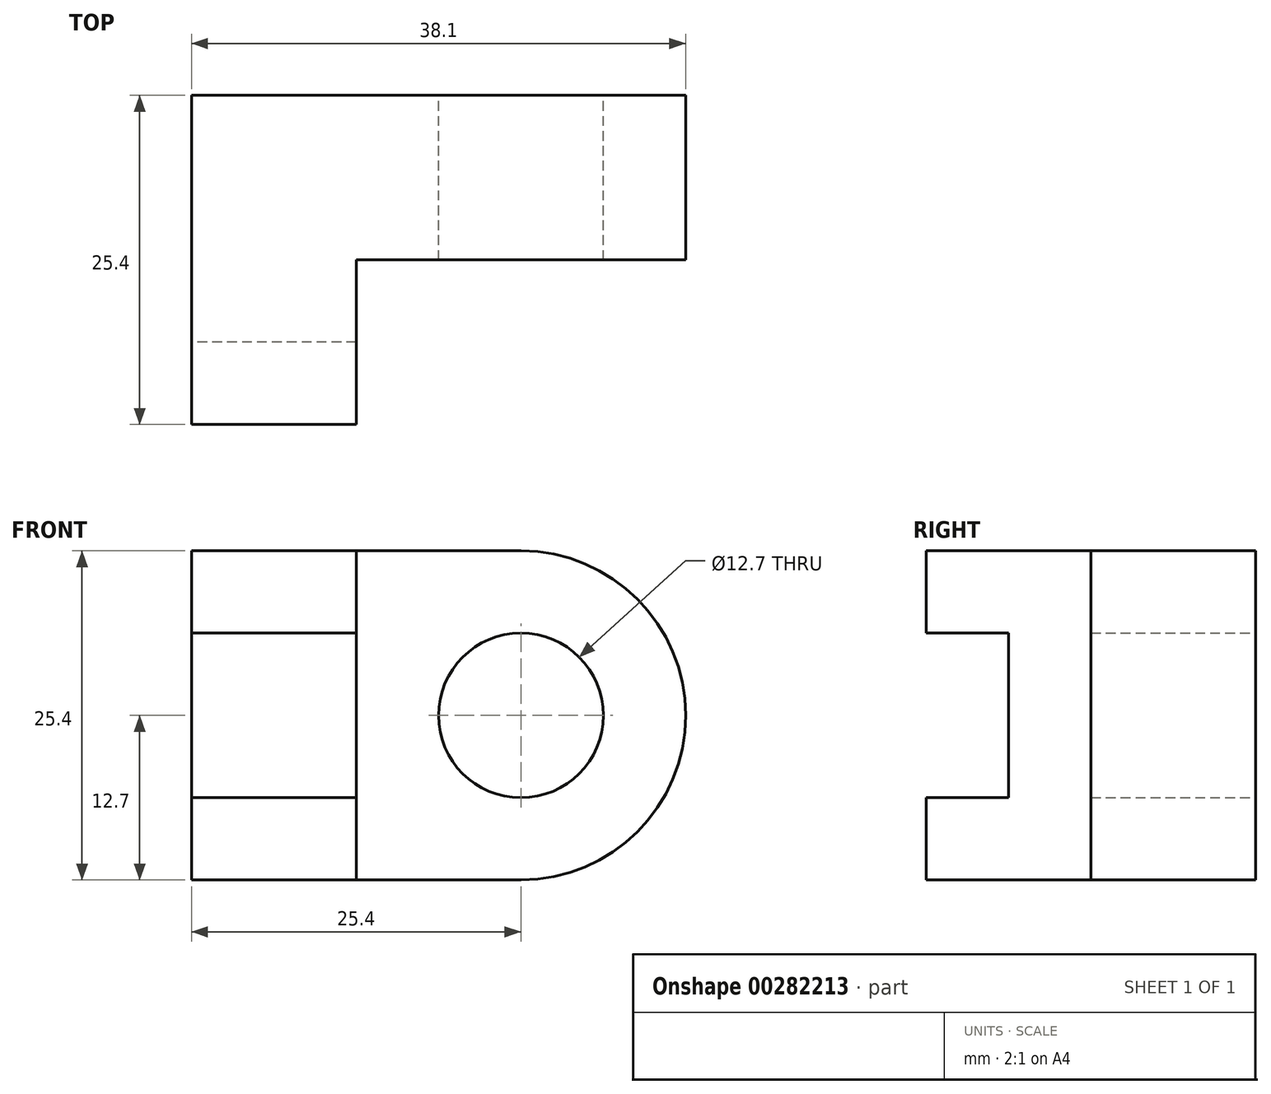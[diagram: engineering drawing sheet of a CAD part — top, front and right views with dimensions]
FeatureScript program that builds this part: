
annotation { "Feature Type Name" : "Feature", "Feature Type Description" : "" }
export const myFeature = defineFeature(function(context is Context, id is Id, definition is map)
    precondition{}
    {
        {
            var Q0;
            Q0=qCreatedBy(makeId("Right.planeOp"),FACE);
            var sketch = newSketch(context, id + "F0", { "sketchPlane" : qUnion([Q0])});
            skLineSegment(sketch, "E0", {"start": v(0, 0) * mm, "end": v(0, 25.4) * mm});
            skLineSegment(sketch, "E1", {"start": v(0, 25.4) * mm, "end": v(-25.4, 25.4) * mm});
            skLineSegment(sketch, "E2", {"start": v(-25.4, 25.4) * mm, "end": v(-25.4, 19.05) * mm});
            skLineSegment(sketch, "E3", {"start": v(-25.4, 19.05) * mm, "end": v(-19.05, 19.05) * mm});
            skLineSegment(sketch, "E4", {"start": v(-19.05, 19.05) * mm, "end": v(-19.05, 6.35) * mm});
            skLineSegment(sketch, "E5", {"start": v(-19.05, 6.35) * mm, "end": v(-25.4, 6.35) * mm});
            skLineSegment(sketch, "E6", {"start": v(-25.4, 6.35) * mm, "end": v(-25.4, 0) * mm});
            skLineSegment(sketch, "E7", {"start": v(-25.4, 0) * mm, "end": v(0, 0) * mm});
            skSolve(sketch);
        }
        {
            var Q0;
            Q0=makeQuery(id+"F0.imprint","IMPRINT",FACE,{"disambiguationData":[TD([[makeQuery(id+"F0.imprint","IMPRINT",EDGE,{"derivedFrom":sQuery(id+"F0.wireOp",EDGE,"E0")}),1.0]])]});
            extrude(context, id + "F1", {"entities" : qUnion([Q0]), "depth" : 12.7 * mm});
        }
        {
            var Q0;
            Q0=qCreatedBy(makeId("Front.planeOp"),FACE);
            var sketch = newSketch(context, id + "F2", { "sketchPlane" : qUnion([Q0])});
            skArc(sketch, "E8", {"start": v(25.4, 0) * mm, "mid": v(38.1, 12.7) * mm, "end": v(25.4, 25.4) * mm});
            skLineSegment(sketch, "E9", {"start": v(25.4, 25.4) * mm, "end": v(12.7, 25.4) * mm});
            skLineSegment(sketch, "E10", {"start": v(12.7, 25.4) * mm, "end": v(12.7, 0) * mm});
            skLineSegment(sketch, "E11", {"start": v(12.7, 0) * mm, "end": v(25.4, 0) * mm});
            skSolve(sketch);
        }
        {
            var Q0;
            Q0=makeQuery(id+"F2.imprint","IMPRINT",FACE,{"disambiguationData":[TD([[makeQuery(id+"F2.imprint","IMPRINT",EDGE,{"derivedFrom":sQuery(id+"F2.wireOp",EDGE,"E8")}),1.0]])]});
            extrude(context, id + "F3", {"entities" : qUnion([Q0]), "operationType" : NewBodyOperationType.ADD, "depth" : 12.7 * mm});
        }
        {
            var Q0;
            Q0=qCreatedBy(makeId("Front.planeOp"),FACE);
            var sketch = newSketch(context, id + "F4", { "sketchPlane" : qUnion([Q0])});
            skCircle(sketch, "E12", {"center": v(25.4, 12.7) * mm, "radius": 6.35 * mm});
            skSolve(sketch);
        }
        {
            var Q0;
            Q0 = qSketchRegion(id + "F4", true);
            extrude(context, id + "F5", {"entities" : qUnion([Q0]), "operationType" : NewBodyOperationType.REMOVE, "depth" : 12.7 * mm});
        }
    });
